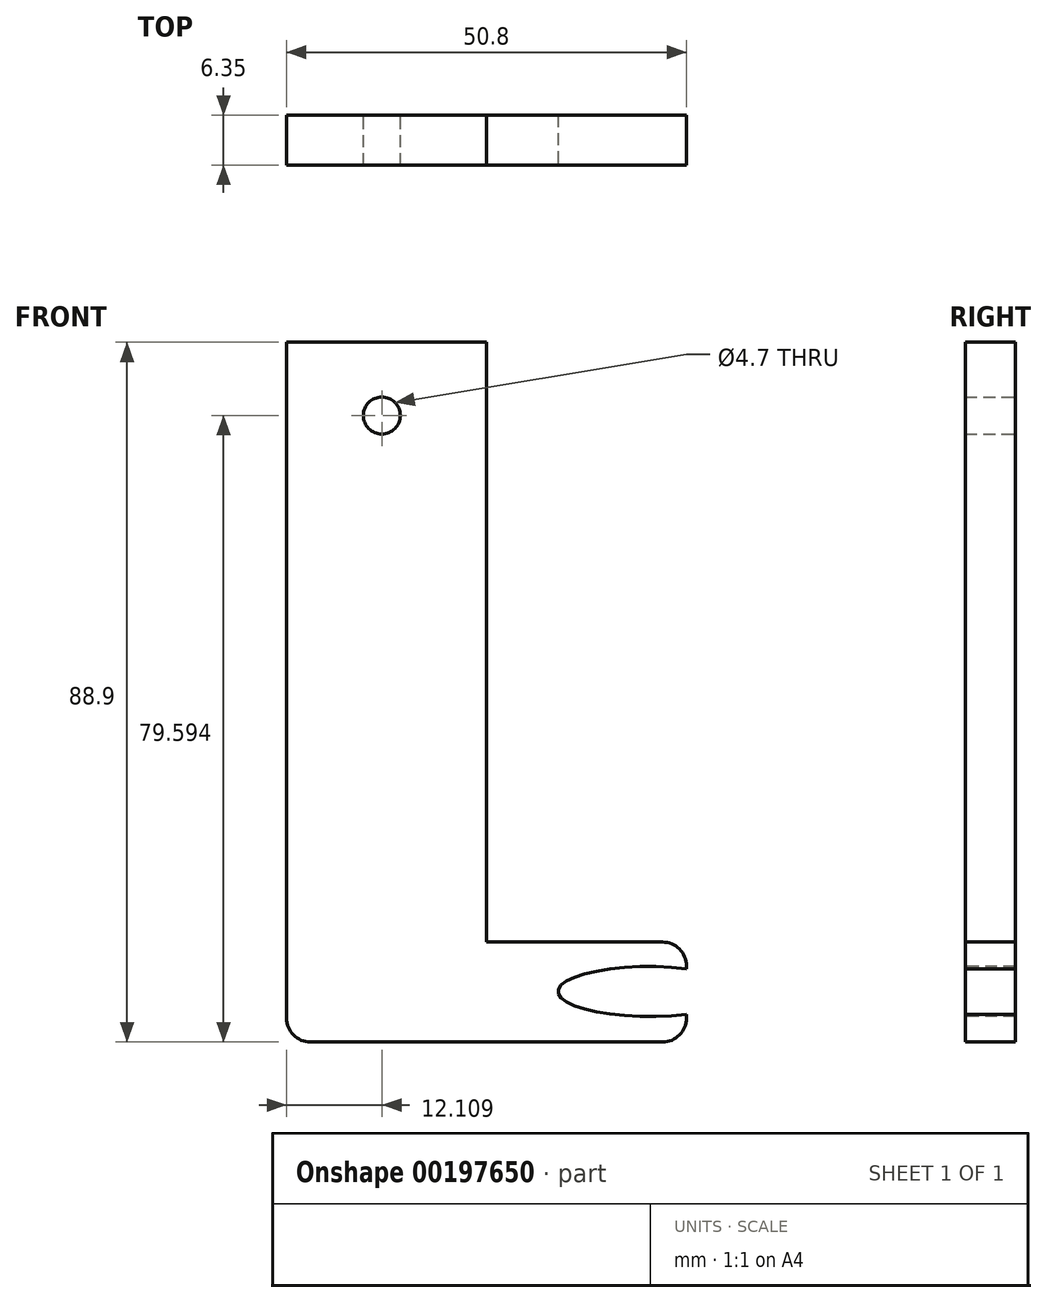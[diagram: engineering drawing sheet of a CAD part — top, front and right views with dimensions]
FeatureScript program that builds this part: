
annotation { "Feature Type Name" : "Feature", "Feature Type Description" : "" }
export const myFeature = defineFeature(function(context is Context, id is Id, definition is map)
    precondition{}
    {
        {
            var Q0;
            Q0=qCreatedBy(makeId("Front.planeOp"),FACE);
            var sketch = newSketch(context, id + "F0", { "sketchPlane" : qUnion([Q0])});
            skLineSegment(sketch, "E0.bottom", {"start": v(-50.8, 48.98) * mm, "end": v(-25.4, 48.98) * mm});
            skLineSegment(sketch, "E0.top", {"start": v(-50.8, -27.22) * mm, "end": v(-25.4, -27.22) * mm});
            skLineSegment(sketch, "E0.left", {"start": v(-50.8, 48.98) * mm, "end": v(-50.8, -27.22) * mm});
            skLineSegment(sketch, "E0.right", {"start": v(-25.4, 48.98) * mm, "end": v(-25.4, -27.22) * mm});
            skLineSegment(sketch, "E1.bottom", {"start": v(-50.8, -27.22) * mm, "end": v(-3.05, -27.22) * mm});
            skLineSegment(sketch, "E1.top", {"start": v(-47.75, -39.92) * mm, "end": v(-3.05, -39.92) * mm});
            skLineSegment(sketch, "E1.left", {"start": v(-50.8, -27.22) * mm, "end": v(-50.8, -36.87) * mm});
            skLineSegment(sketch, "E1.right", {"start": v(0, -30.26) * mm, "end": v(0, -36.87) * mm});
            skEllipse(sketch, "E2", {"center": v(-4.73, -33.5) * mm, "majorRadius": 11.59 * mm, "minorRadius": 3.18 * mm, "majorAxis": v(1, 0)});
            skPoint(sketch, "E3.visualSharp", {"position": v(0, -27.22) * mm});
            skArc(sketch, "E3.filletArc", {"start": v(0, -30.26) * mm, "mid": v(-0.9, -28.1) * mm, "end": v(-3.05, -27.22) * mm});
            skPoint(sketch, "E4.visualSharp", {"position": v(0, -39.92) * mm});
            skArc(sketch, "E4.filletArc", {"start": v(-3.05, -39.92) * mm, "mid": v(-0.9, -39.02) * mm, "end": v(0, -36.87) * mm});
            skPoint(sketch, "E5.visualSharp", {"position": v(-50.8, -39.92) * mm});
            skArc(sketch, "E5.filletArc", {"start": v(-50.8, -36.87) * mm, "mid": v(-49.9, -39.02) * mm, "end": v(-47.75, -39.92) * mm});
            skCircle(sketch, "E6", {"center": v(-38.7, 39.67) * mm, "radius": 2.35 * mm});
            skSolve(sketch);
        }
        {
            var Q0;
            Q0=makeQuery(id+"F0.imprint","IMPRINT",FACE,{"disambiguationData":[TD([[makeQuery(id+"F0.imprint","IMPRINT",EDGE,{"derivedFrom":sQuery(id+"F0.wireOp",EDGE,"E0.bottom")}),-1.0]])]});
            var Q1;
            Q1=makeQuery(id+"F0.imprint","IMPRINT",FACE,{"disambiguationData":[TD([[makeQuery(id+"F0.imprint","IMPRINT",EDGE,{"derivedFrom":sQuery(id+"F0.wireOp",EDGE,"E1.top")}),1.0]])]});
            extrude(context, id + "F1", {"entities" : qUnion([Q0, Q1]), "depth" : 6.35 * mm});
        }
    });
